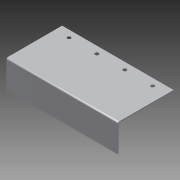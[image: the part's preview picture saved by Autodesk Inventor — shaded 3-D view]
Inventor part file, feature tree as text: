
AUTODESK INVENTOR PART (.ipt)
format: ipt  version: 2013 (Build 170138000, 138)  size: 108,032 bytes
history: native  units: in
note: dims shown in document units (in); Inventor stores cm internally (conversion verified against a paired STEP export)
features: sheet_metal_op x4, sketch x2, other x2
ambient origin geometry x8: Origin, YZ Plane, XZ Plane, XY Plane, X Axis, Y Axis, Z Axis, Center Point
bodies: Solid1 (feature_tree)
feature tree (8):
  sheet_metal_op  "Face1"
  sheet_metal_op  "Flange1"
  sketch  "Sketch1"  dims[d0=2.0in]
  other  "Plate1"
  sketch  "Sketch2"  dims[d1=0.26in d2=0.26in d3=1.0in d4=2.0in d6=2.0in d7=2.0in d8=3.0in d9=8.0in d10=0.0625in d11=0.0625in d12=0.0312in d13=0.125in d14=0.0625in d15=2.0in d16=90.0deg d17=0.05in d18=0.25in d19=0.0625in d20=0.0625in]
  other  "Plate2"
  sheet_metal_op  "Bend1"
  sheet_metal_op  "Corner1"
